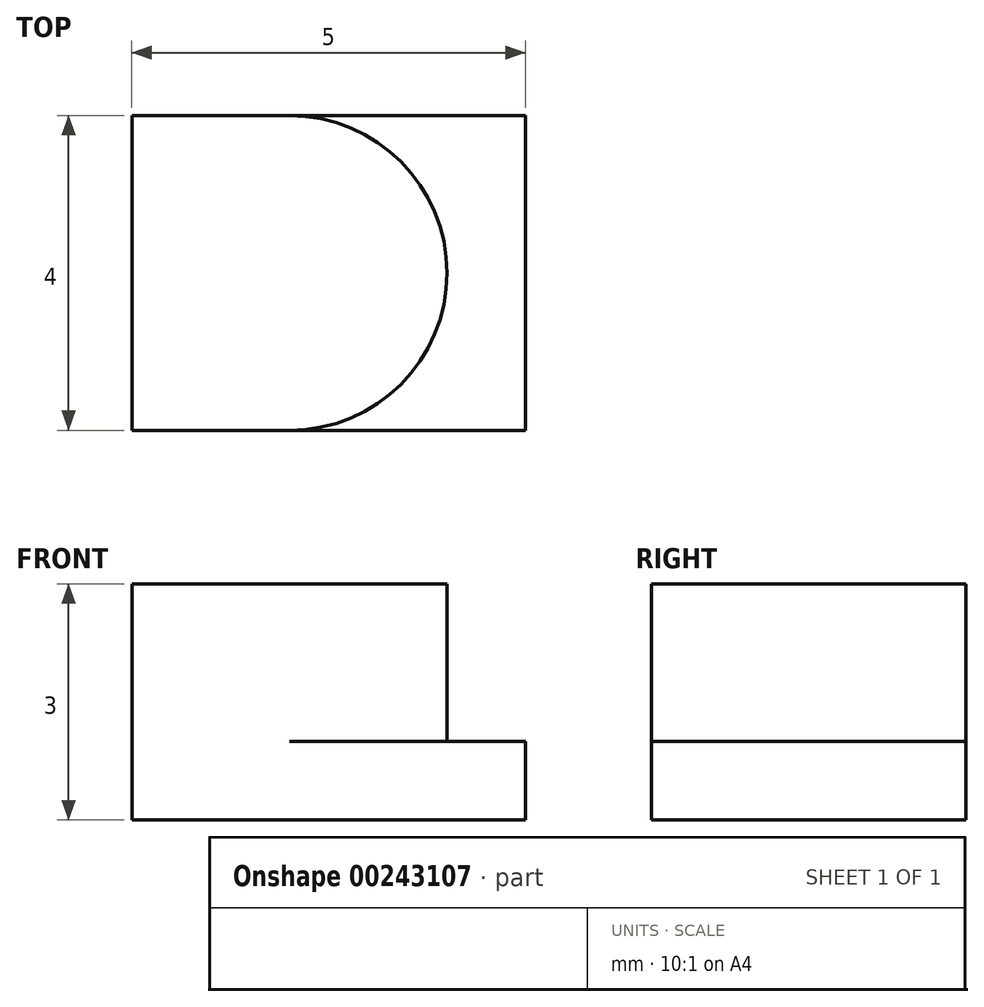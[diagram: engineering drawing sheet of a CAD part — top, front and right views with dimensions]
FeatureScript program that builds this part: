
annotation { "Feature Type Name" : "Feature", "Feature Type Description" : "" }
export const myFeature = defineFeature(function(context is Context, id is Id, definition is map)
    precondition{}
    {
        {
            var Q0;
            Q0=qCreatedBy(makeId("Top.planeOp"),FACE);
            var sketch = newSketch(context, id + "F0", { "sketchPlane" : qUnion([Q0])});
            skLineSegment(sketch, "E0.bottom", {"start": v(8.34, 14.14) * mm, "end": v(13.34, 14.14) * mm});
            skLineSegment(sketch, "E0.top", {"start": v(8.34, 10.14) * mm, "end": v(13.34, 10.14) * mm});
            skLineSegment(sketch, "E0.left", {"start": v(8.34, 14.14) * mm, "end": v(8.34, 10.14) * mm});
            skLineSegment(sketch, "E0.right", {"start": v(13.34, 14.14) * mm, "end": v(13.34, 10.14) * mm});
            skSolve(sketch);
        }
        {
            var Q0;
            Q0 = qSketchRegion(id + "F0", true);
            extrude(context, id + "F1", {"entities" : qUnion([Q0]), "depth" : 1 * mm});
        }
        {
            var Q0;
            Q0=makeQuery(id+"F1.opExtrude","CAP_FACE",FACE,{"disambiguationData":[OSD([sQuery(id+"F0.wireOp",EDGE,"E0.bottom"),sQuery(id+"F0.wireOp",EDGE,"E0.top"),sQuery(id+"F0.wireOp",EDGE,"E0.left"),sQuery(id+"F0.wireOp",EDGE,"E0.right")])],"isStart":false});
            var sketch = newSketch(context, id + "F2", { "sketchPlane" : qUnion([Q0])});
            skPoint(sketch, "E1.0", {"position": v(8.34, 14.14) * mm});
            skPoint(sketch, "E1.1", {"position": v(8.34, 10.14) * mm});
            skPoint(sketch, "E1.2", {"position": v(13.34, 14.14) * mm});
            skPoint(sketch, "E1.3", {"position": v(13.34, 10.14) * mm});
            skLineSegment(sketch, "E2", {"start": v(8.34, 14.14) * mm, "end": v(8.34, 10.14) * mm});
            skLineSegment(sketch, "E3", {"start": v(8.34, 10.14) * mm, "end": v(10.34, 10.14) * mm});
            skLineSegment(sketch, "E4", {"start": v(10.34, 14.14) * mm, "end": v(8.34, 14.14) * mm});
            skCircle(sketch, "E5", {"center": v(10.34, 12.14) * mm, "radius": 2 * mm});
            skSolve(sketch);
        }
        {
            var Q0;
            Q0 = qSketchRegion(id + "F2", true);
            extrude(context, id + "F3", {"entities" : qUnion([Q0]), "operationType" : NewBodyOperationType.ADD, "depth" : 2 * mm});
        }
    });
